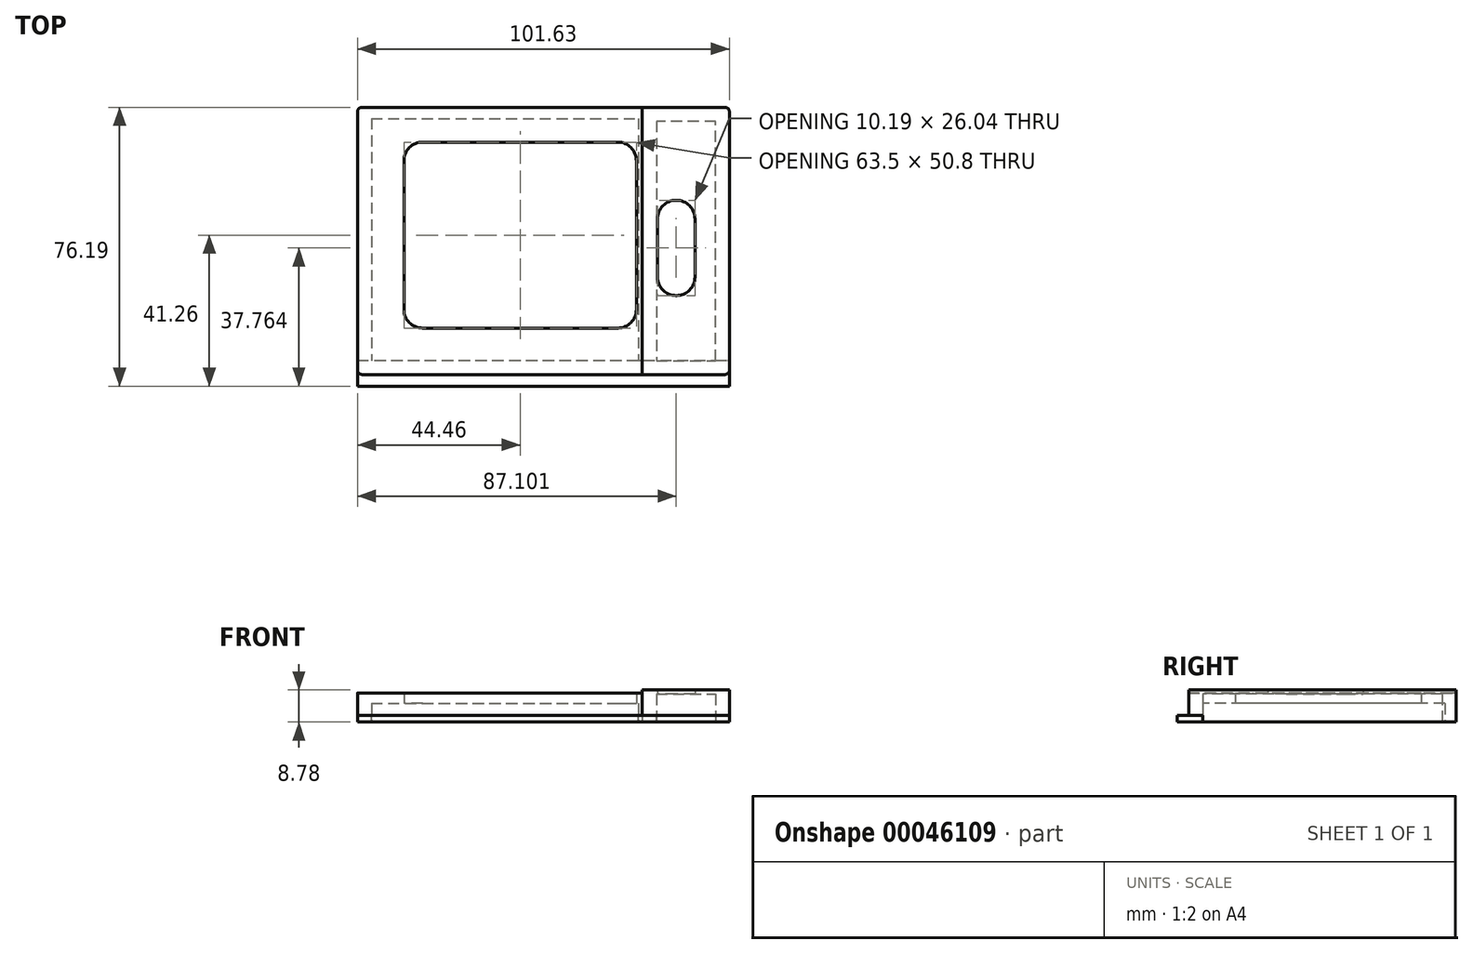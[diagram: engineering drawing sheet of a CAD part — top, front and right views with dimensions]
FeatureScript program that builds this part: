
annotation { "Feature Type Name" : "Feature", "Feature Type Description" : "" }
export const myFeature = defineFeature(function(context is Context, id is Id, definition is map)
    precondition{}
    {
        {
            var Q0;
            Q0=qCreatedBy(makeId("Top.planeOp"),FACE);
            var sketch = newSketch(context, id + "F0", { "sketchPlane" : qUnion([Q0])});
            skLineSegment(sketch, "E0", {"start": v(-31.75, 25.4) * mm, "end": v(31.75, 25.4) * mm});
            skLineSegment(sketch, "E1.MirrorCS", {"start": v(-31.75, -25.4) * mm, "end": v(31.75, -25.4) * mm});
            skLineSegment(sketch, "E2", {"start": v(-31.75, 25.4) * mm, "end": v(-31.75, -25.4) * mm});
            skLineSegment(sketch, "E3", {"start": v(31.75, 25.4) * mm, "end": v(31.75, -25.4) * mm});
            skPoint(sketch, "E4.endSnap0", {"position": v(0, 25.4) * mm});
            skPoint(sketch, "E5.endSnap0", {"position": v(-31.75, 0) * mm});
            skPoint(sketch, "E6.endSnap0", {"position": v(31.75, 0) * mm});
            skLineSegment(sketch, "E7", {"start": v(-44.46, 34.93) * mm, "end": v(-44.46, -38.1) * mm});
            skLineSegment(sketch, "E8", {"start": v(-44.46, -38.1) * mm, "end": v(33.34, -38.1) * mm});
            skLineSegment(sketch, "E9", {"start": v(33.34, -38.1) * mm, "end": v(33.34, 34.93) * mm});
            skLineSegment(sketch, "E10", {"start": v(33.34, 34.93) * mm, "end": v(-44.46, 34.93) * mm});
            skLineSegment(sketch, "E11", {"start": v(33.34, 34.93) * mm, "end": v(57.17, 34.93) * mm});
            skLineSegment(sketch, "E12", {"start": v(57.17, 34.93) * mm, "end": v(57.17, -38.1) * mm});
            skLineSegment(sketch, "E13", {"start": v(57.17, -38.1) * mm, "end": v(33.34, -38.1) * mm});
            skLineSegment(sketch, "E14", {"start": v(37.54, -16.51) * mm, "end": v(37.54, 9.52) * mm});
            skLineSegment(sketch, "E15", {"start": v(37.54, 9.52) * mm, "end": v(47.74, 9.52) * mm});
            skLineSegment(sketch, "E16", {"start": v(47.74, 9.52) * mm, "end": v(47.74, -16.51) * mm});
            skLineSegment(sketch, "E17", {"start": v(47.74, -16.51) * mm, "end": v(37.54, -16.51) * mm});
            skSolve(sketch);
        }
        {
            var Q0;
            Q0=makeQuery(id+"F0.imprint","IMPRINT",FACE,{"disambiguationData":[TD([[makeQuery(id+"F0.imprint","IMPRINT",EDGE,{"derivedFrom":sQuery(id+"F0.wireOp",EDGE,"E0")}),1.0]])]});
            extrude(context, id + "F1", {"entities" : qUnion([Q0]), "depth" : 7.94 * mm});
        }
        {
            var Q0;
            Q0=makeQuery(id+"F0.imprint","IMPRINT",FACE,{"disambiguationData":[TD([[makeQuery(id+"F0.imprint","IMPRINT",EDGE,{"derivedFrom":sQuery(id+"F0.wireOp",EDGE,"E9")}),-1.0]])]});
            extrude(context, id + "F2", {"entities" : qUnion([Q0]), "depth" : 8.78 * mm});
        }
        {
            var Q0;
            Q0=makeQuery(id+"F0.imprint","IMPRINT",FACE,{"disambiguationData":[TD([[makeQuery(id+"F0.imprint","IMPRINT",EDGE,{"derivedFrom":sQuery(id+"F0.wireOp",EDGE,"E0")}),1.0]])]});
            var sketch = newSketch(context, id + "F3", { "sketchPlane" : qUnion([Q0])});
            skLineSegment(sketch, "E18", {"start": v(33.34, 0) * mm, "end": v(32.32, 0) * mm});
            skLineSegment(sketch, "E19", {"start": v(-40.65, 31.86) * mm, "end": v(-40.65, -34.3) * mm});
            skLineSegment(sketch, "E20", {"start": v(-40.65, 31.86) * mm, "end": v(32.32, 31.86) * mm});
            skLineSegment(sketch, "E21", {"start": v(32.32, 31.86) * mm, "end": v(32.32, -34.3) * mm});
            skLineSegment(sketch, "E22", {"start": v(32.32, -34.3) * mm, "end": v(-40.65, -34.3) * mm});
            skSolve(sketch);
        }
        {
            var Q0;
            Q0 = qSketchRegion(id + "F3", true);
            extrude(context, id + "F4", {"entities" : qUnion([Q0]), "operationType" : NewBodyOperationType.REMOVE, "depth" : 5.08 * mm});
        }
        {
            var Q0;
            Q0=makeQuery(id+"F0.imprint","IMPRINT",FACE,{"disambiguationData":[TD([[makeQuery(id+"F0.imprint","IMPRINT",EDGE,{"derivedFrom":sQuery(id+"F0.wireOp",EDGE,"E9")}),-1.0]])]});
            var sketch = newSketch(context, id + "F5", { "sketchPlane" : qUnion([Q0])});
            skLineSegment(sketch, "E23", {"start": v(53.41, -34.33) * mm, "end": v(53.41, 31.12) * mm});
            skLineSegment(sketch, "E24", {"start": v(53.41, 31.12) * mm, "end": v(37.2, 31.12) * mm});
            skLineSegment(sketch, "E25", {"start": v(37.2, 31.12) * mm, "end": v(37.2, -34.33) * mm});
            skLineSegment(sketch, "E26", {"start": v(37.2, -34.33) * mm, "end": v(53.41, -34.33) * mm});
            skSolve(sketch);
        }
        {
            var Q0;
            Q0 = qSketchRegion(id + "F5", true);
            extrude(context, id + "F6", {"entities" : qUnion([Q0]), "operationType" : NewBodyOperationType.REMOVE, "depth" : 7.62 * mm});
        }
        {
            var Q0;
            Q0=makeQuery(id+"F0.imprint","IMPRINT",FACE,{"disambiguationData":[TD([[makeQuery(id+"F0.imprint","IMPRINT",EDGE,{"derivedFrom":sQuery(id+"F0.wireOp",EDGE,"E0")}),1.0]])]});
            var sketch = newSketch(context, id + "F7", { "sketchPlane" : qUnion([Q0])});
            skLineSegment(sketch, "E27", {"start": v(-44.46, -41.26) * mm, "end": v(57.17, -41.26) * mm});
            skLineSegment(sketch, "E28.MirrorCS", {"start": v(-44.46, -34.25) * mm, "end": v(57.17, -34.25) * mm});
            skLineSegment(sketch, "E29", {"start": v(-44.46, -41.26) * mm, "end": v(-44.46, -34.25) * mm});
            skLineSegment(sketch, "E30", {"start": v(57.17, -41.26) * mm, "end": v(57.17, -34.25) * mm});
            skSolve(sketch);
        }
        {
            var Q0;
            Q0 = qSketchRegion(id + "F7", true);
            extrude(context, id + "F8", {"entities" : qUnion([Q0]), "operationType" : NewBodyOperationType.REMOVE, "depth" : 1.78 * mm});
        }
        {
            var Q0;
            Q0=makeQuery(id+"F7.imprint","IMPRINT",FACE,{"disambiguationData":[TD([[makeQuery(id+"F7.imprint","IMPRINT",EDGE,{"derivedFrom":sQuery(id+"F7.wireOp",EDGE,"E27")}),1.0]])]});
            var Q1;
            {var subQ5=makeQuery(id+"F0.imprint","IMPRINT",EDGE,{"derivedFrom":sQuery(id+"F0.wireOp",EDGE,"E8")});Q1=makeQuery(id+"F7.imprint","IMPRINT",FACE,{"disambiguationData":[TD([[makeQuery(id+"F7.imprint","IMPRINT",EDGE,{"derivedFrom":subQ5}),1.0]])]});}
            extrude(context, id + "F9", {"entities" : qUnion([Q0, Q1]), "depth" : 1.78 * mm});
        }
        {
            var Q0;
            Q0=makeQuery(id+"F1.opExtrude","SWEPT_EDGE",EDGE,{"disambiguationData":[OSD([sQuery(id+"F0.wireOp",EDGE,"E0"),sQuery(id+"F0.wireOp",EDGE,"E3")])]});
            var Q1;
            Q1=makeQuery(id+"F1.opExtrude","SWEPT_EDGE",EDGE,{"disambiguationData":[OSD([sQuery(id+"F0.wireOp",EDGE,"E0"),sQuery(id+"F0.wireOp",EDGE,"E2")])]});
            var Q2;
            Q2=makeQuery(id+"F1.opExtrude","SWEPT_EDGE",EDGE,{"disambiguationData":[OSD([sQuery(id+"F0.wireOp",EDGE,"E1.MirrorCS"),sQuery(id+"F0.wireOp",EDGE,"E3")])]});
            var Q3;
            Q3=makeQuery(id+"F1.opExtrude","SWEPT_EDGE",EDGE,{"disambiguationData":[OSD([sQuery(id+"F0.wireOp",EDGE,"E1.MirrorCS"),sQuery(id+"F0.wireOp",EDGE,"E2")])]});
            fillet(context, id + "F10", {"entities" : qUnion([Q0, Q1, Q2, Q3]), "radius" : 5.08 * mm, "tangentPropagation" : true, "allowEdgeOverflow" : false});
        }
        {
            var Q0;
            Q0=makeQuery(id+"F2.opExtrude","SWEPT_EDGE",EDGE,{"disambiguationData":[OSD([sQuery(id+"F0.wireOp",EDGE,"E14"),sQuery(id+"F0.wireOp",EDGE,"85e538f0-3094-427d-b745-fc8beb3b7a1e")])]});
            var Q1;
            Q1=makeQuery(id+"F2.opExtrude","SWEPT_EDGE",EDGE,{"disambiguationData":[OSD([sQuery(id+"F0.wireOp",EDGE,"85e538f0-3094-427d-b745-fc8beb3b7a1e"),sQuery(id+"F0.wireOp",EDGE,"8080c24b-df8b-4ccf-884a-0ed01abe4ebf")])]});
            var Q2;
            Q2=makeQuery(id+"F2.opExtrude","SWEPT_EDGE",EDGE,{"disambiguationData":[OSD([sQuery(id+"F0.wireOp",EDGE,"E14"),sQuery(id+"F0.wireOp",EDGE,"7f57950d-e123-4f4a-9cfe-cbf7c64db301")])]});
            var Q3;
            Q3=makeQuery(id+"F2.opExtrude","SWEPT_EDGE",EDGE,{"disambiguationData":[OSD([sQuery(id+"F0.wireOp",EDGE,"8080c24b-df8b-4ccf-884a-0ed01abe4ebf"),sQuery(id+"F0.wireOp",EDGE,"7f57950d-e123-4f4a-9cfe-cbf7c64db301")])]});
            var Q4;
            Q4=makeQuery(id+"F2.opExtrude","SWEPT_EDGE",EDGE,{"disambiguationData":[OSD([sQuery(id+"F0.wireOp",EDGE,"E15"),sQuery(id+"F0.wireOp",EDGE,"E16")])]});
            var Q5;
            Q5=makeQuery(id+"F2.opExtrude","SWEPT_EDGE",EDGE,{"disambiguationData":[OSD([sQuery(id+"F0.wireOp",EDGE,"E16"),sQuery(id+"F0.wireOp",EDGE,"E17")])]});
            fillet(context, id + "F11", {"entities" : qUnion([Q0, Q1, Q2, Q3, Q4, Q5]), "radius" : 5.08 * mm, "tangentPropagation" : true, "allowEdgeOverflow" : false});
        }
        {
            var Q0;
            Q0=makeQuery(id+"F2.opExtrude","SWEPT_EDGE",EDGE,{"disambiguationData":[OSD([sQuery(id+"F0.wireOp",EDGE,"E11"),sQuery(id+"F0.wireOp",EDGE,"E12")])]});
            var Q1;
            Q1=makeQuery(id+"F1.opExtrude","SWEPT_EDGE",EDGE,{"disambiguationData":[OSD([sQuery(id+"F0.wireOp",EDGE,"E7"),sQuery(id+"F0.wireOp",EDGE,"E10")])]});
            var Q2;
            Q2=makeQuery(id+"F2.opExtrude","SWEPT_EDGE",EDGE,{"disambiguationData":[OSD([sQuery(id+"F0.wireOp",EDGE,"E12"),sQuery(id+"F0.wireOp",EDGE,"E13")])]});
            var Q3;
            Q3=makeQuery(id+"F1.opExtrude","SWEPT_EDGE",EDGE,{"disambiguationData":[OSD([sQuery(id+"F0.wireOp",EDGE,"E7"),sQuery(id+"F0.wireOp",EDGE,"E8")])]});
            fillet(context, id + "F12", {"entities" : qUnion([Q0, Q1, Q2, Q3]), "radius" : 1.27 * mm, "tangentPropagation" : true, "allowEdgeOverflow" : false});
        }
    });
